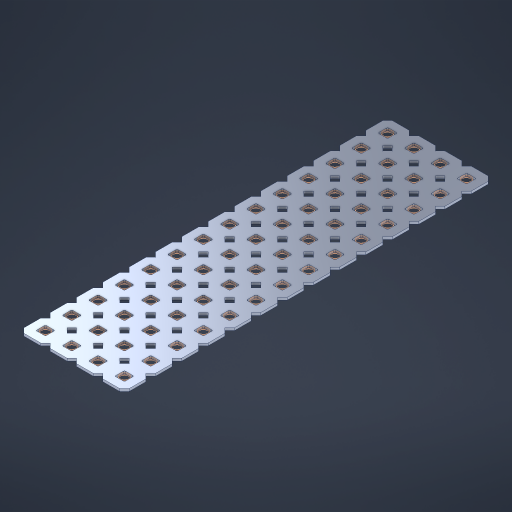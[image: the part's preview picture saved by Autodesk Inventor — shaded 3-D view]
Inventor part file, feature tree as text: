
AUTODESK INVENTOR PART (.ipt)
format: ipt  version: 2023 (Build 270158000, 158)  size: 908,800 bytes
history: native  units: in
note: dims shown in document units (in); Inventor stores cm internally (conversion verified against a paired STEP export)
features: other x57, extrude x55, sketch x2, pattern_linear x1
ambient origin geometry x8: Origin, YZ Plane, XZ Plane, XY Plane, X Axis, Y Axis, Z Axis, Center Point
bodies: Solid1 (feature_tree), Body (feature_tree)
feature tree (115):
  pattern_linear  "Rectangular Pattern1"  Spacing1=0.09in  [1 undecoded]
  sketch  "Sketch1"  dims[d1=0.5in]
  sketch  "Sketch2"  dims[d2=0.182in d3=0.09in d4=0.09in d5=0.09in d6=0.09in d7=0.09in d8=0.09in d9=0.09in d10=0.09in d11=0.02in d13=0.0in d14=0.172in d15=0.0625in d16=0.0in d19=0.5in d22=0.5in]
  other  "Srf1"
  other  "Srf126"
  other  "Srf127"
  other  "Srf128"
  other  "Srf129"
  other  "Srf130"
  other  "Srf131"
  other  "Srf250"
  other  "Srf251"
  other  "Srf252"
  other  "Srf253"
  other  "Srf254"
  other  "Srf255"
  other  "Srf256"
  other  "Srf268"
  other  "Srf269"
  other  "Srf270"
  other  "Srf271"
  other  "Srf272"
  other  "Srf273"
  other  "Srf274"
  other  "Srf275"
  other  "Srf276"
  other  "Srf277"
  other  "Srf278"
  other  "Srf279"
  other  "Srf280"
  other  "Srf281"
  other  "Srf293"
  other  "Srf294"
  other  "Srf295"
  other  "Srf296"
  other  "Srf297"
  other  "Srf298"
  other  "Srf299"
  other  "Srf300"
  other  "Srf301"
  other  "Srf302"
  other  "Srf303"
  other  "Srf304"
  other  "Srf305"
  other  "Srf306"
  other  "Srf318"
  other  "Srf319"
  other  "Srf320"
  other  "Srf321"
  other  "Srf322"
  other  "Srf323"
  other  "Srf324"
  other  "Srf325"
  other  "Srf326"
  other  "Srf327"
  other  "Srf328"
  other  "Srf329"
  other  "Srf330"
  other  "Srf331"
  other  "Circle"
  extrude  "ExtrusionSrf126"  Depth=0.09in
  extrude  "ExtrusionSrf127"  Depth=0.09in
  extrude  "ExtrusionSrf128"  Depth=0.09in
  extrude  "ExtrusionSrf129"  Depth=0.09in
  extrude  "ExtrusionSrf130"  Depth=0.09in
  extrude  "ExtrusionSrf131"  Depth=0.09in
  extrude  "ExtrusionSrf250"  Depth=0.09in
  extrude  "ExtrusionSrf251"  Depth=0.02in
  extrude  "ExtrusionSrf252"  TaperAngle=0.0deg  [1 undecoded]
  extrude  "ExtrusionSrf253"  Depth=0.5in
  extrude  "ExtrusionSrf254"  Depth=0.5in TaperAngle=0.0deg
  extrude  "ExtrusionSrf255"  Depth=0.5in
  extrude  "ExtrusionSrf256"  Depth=0.5in
  extrude  "ExtrusionSrf268"  [1 undecoded]
  extrude  "ExtrusionSrf269"  [1 undecoded]
  extrude  "ExtrusionSrf270"  [1 undecoded]
  extrude  "ExtrusionSrf271"  [1 undecoded]
  extrude  "ExtrusionSrf272"  [1 undecoded]
  extrude  "ExtrusionSrf273"  [1 undecoded]
  extrude  "ExtrusionSrf274"  [1 undecoded]
  extrude  "ExtrusionSrf275"  [1 undecoded]
  extrude  "ExtrusionSrf276"  [1 undecoded]
  extrude  "ExtrusionSrf277"  [1 undecoded]
  extrude  "ExtrusionSrf278"  [1 undecoded]
  extrude  "ExtrusionSrf279"  [1 undecoded]
  extrude  "ExtrusionSrf280"  [1 undecoded]
  extrude  "ExtrusionSrf281"  [1 undecoded]
  extrude  "ExtrusionSrf293"  [1 undecoded]
  extrude  "ExtrusionSrf294"  [1 undecoded]
  extrude  "ExtrusionSrf295"  [1 undecoded]
  extrude  "ExtrusionSrf296"  [1 undecoded]
  extrude  "ExtrusionSrf297"  [1 undecoded]
  extrude  "ExtrusionSrf298"  [1 undecoded]
  extrude  "ExtrusionSrf299"  [1 undecoded]
  extrude  "ExtrusionSrf300"  [1 undecoded]
  extrude  "ExtrusionSrf301"  [1 undecoded]
  extrude  "ExtrusionSrf302"  [1 undecoded]
  extrude  "ExtrusionSrf303"  [1 undecoded]
  extrude  "ExtrusionSrf304"  [1 undecoded]
  extrude  "ExtrusionSrf305"  [1 undecoded]
  extrude  "ExtrusionSrf306"  [1 undecoded]
  extrude  "ExtrusionSrf318"  [1 undecoded]
  extrude  "ExtrusionSrf319"  [1 undecoded]
  extrude  "ExtrusionSrf320"  [1 undecoded]
  extrude  "ExtrusionSrf321"  [1 undecoded]
  extrude  "ExtrusionSrf322"  [1 undecoded]
  extrude  "ExtrusionSrf323"  [1 undecoded]
  extrude  "ExtrusionSrf324"  [1 undecoded]
  extrude  "ExtrusionSrf325"  [1 undecoded]
  extrude  "ExtrusionSrf326"  [1 undecoded]
  extrude  "ExtrusionSrf327"  [1 undecoded]
  extrude  "ExtrusionSrf328"  [1 undecoded]
  extrude  "ExtrusionSrf329"  [1 undecoded]
  extrude  "ExtrusionSrf330"  [1 undecoded]
  extrude  "ExtrusionSrf331"  [1 undecoded]
note: 44 required parameter values undecoded (feature->parameter linkage not recoverable at this tier; creation-order binding heuristic only, values carry confidence <= 0.55)
